# Revit family: AKTQ24T
name_source: partatom
category: Lighting Fixtures
revit_build: Autodesk Revit Architecture 2012 (Build: 20110309_2315(x64)
units: mm (PartAtom-declared; Revit-internal decimal feet)

## types (1)
- AKTQ24T
    Blades = Steel Grey powder coated galvanized steel
    Color Filter = 16777215
    Default Elevation = 48"
    Description = Two 24W Linear T-5 HO Lamps
    Dimming Lamp Color Temperature Shift = <None>
    Emit from Line Length = 20"
    Family = Quest 24" Wall Wash
    Finish = Honeycomb embossed Aluminium
    Lamp = T-5 HO
    Manufacturer = Prescolite
    Manufacturer Fax = 864-678-1065
    Model = AKTQ24T
    Pendant Length = 2"
    Photometric Web File = generic
    Product Documentation Link = http://www.prescolite.com
    Product Page URL = http://www.prescolite.com
    Tilt Angle = -90.00°
    URL = http://www.prescolite.com
    Wattage Comments = 24W

## geometry (parser evidence)
native form markers: Sweep x5
no freeform markers — native parametric forms only
